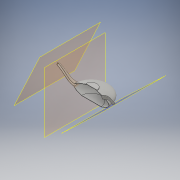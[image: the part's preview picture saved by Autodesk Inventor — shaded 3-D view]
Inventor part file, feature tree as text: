
AUTODESK INVENTOR PART (.ipt)
format: ipt  version: 2016 (Build 200138000, 138)  size: 432,640 bytes
history: native  units: in
note: dims shown in document units (in); Inventor stores cm internally (conversion verified against a paired STEP export)
features: sketch x6, plane x3, other x1, revolve x1, loft x1, shell x1, sweep x1
ambient origin geometry x8: Origin, YZ Plane, XZ Plane, XY Plane, X Axis, Y Axis, Z Axis, Center Point
bodies: Solid1 (feature_tree)
feature tree (14):
  other  "CrossSection1"
  revolve  "Revolution1"  [1 undecoded]
  sketch  "Sketch2"  dims[d9=0.0in d10=90.0deg d11=0.0in d12=90.0deg d13=0.0in d14=90.0deg]
  plane  "Work Plane1"
  sketch  "Sketch4"
  plane  "Work Plane2"
  plane  "Work Plane3"
  loft  "Loft2"
  shell  "Shell1"  Thickness=0.0in
  sweep  "Sweep1"
  sketch  "Sketch1"  dims[d0=90.0deg d1=0.0in d2=0.0in]
  sketch  "Sketch3"  dims[d15=0.005in d16=0.013in d17=0.5in d18=0.0in d19=2.0in]
  sketch  "Sketch10"
  sketch  "Sketch11"
note: 1 required parameter value undecoded (feature->parameter linkage not recoverable at this tier; creation-order binding heuristic only, values carry confidence <= 0.55)
